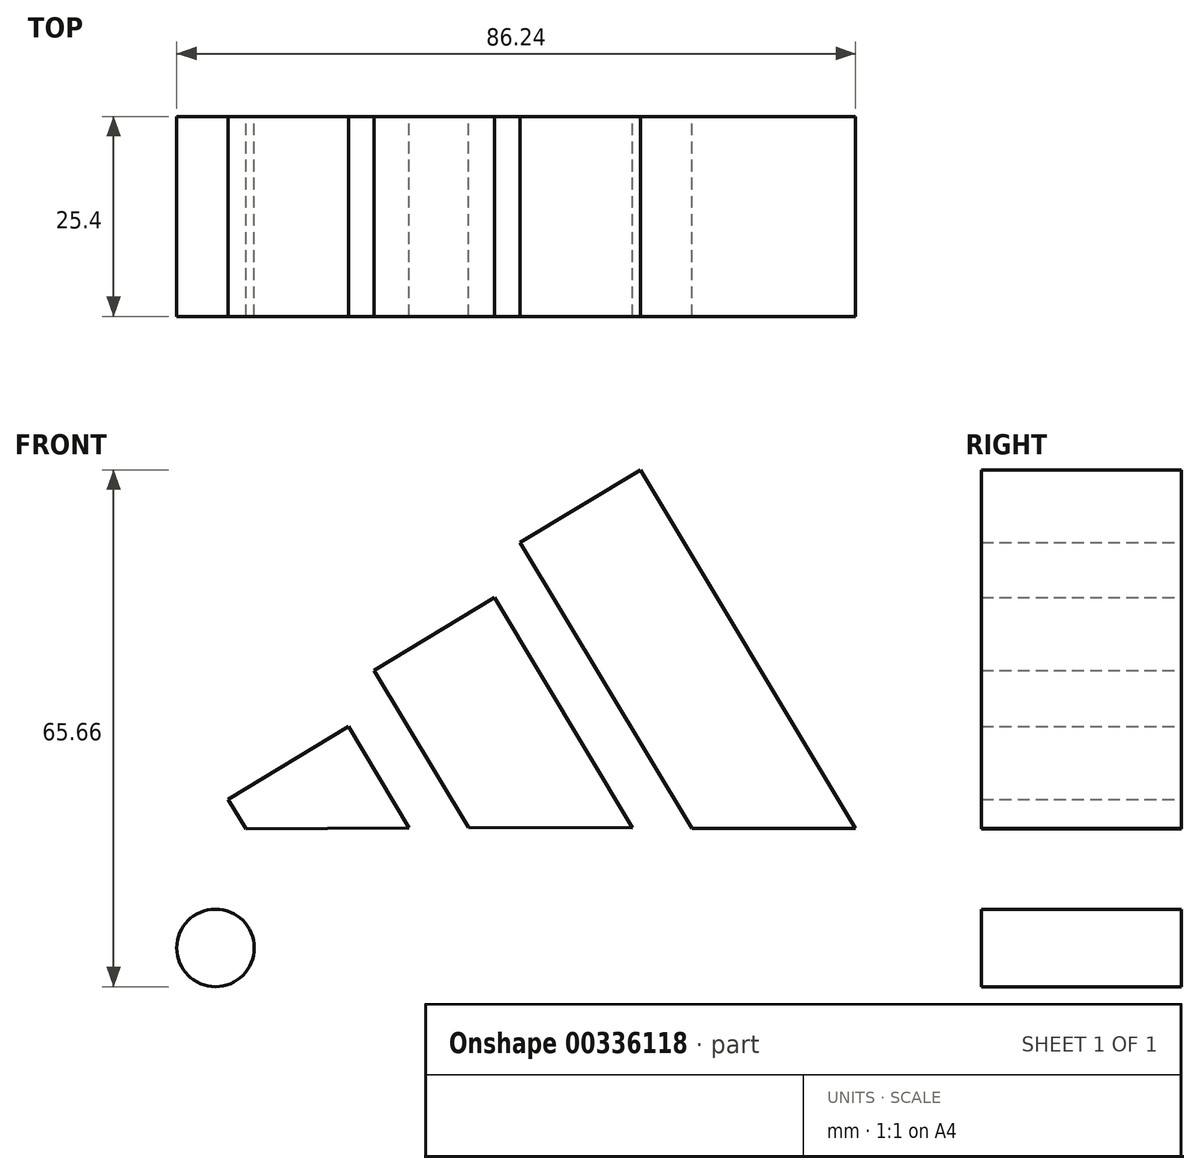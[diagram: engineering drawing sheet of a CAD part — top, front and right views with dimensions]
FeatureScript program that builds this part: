
annotation { "Feature Type Name" : "Feature", "Feature Type Description" : "" }
export const myFeature = defineFeature(function(context is Context, id is Id, definition is map)
    precondition{}
    {
        {
            var Q0;
            Q0=qCreatedBy(makeId("Front.planeOp"),FACE);
            var sketch = newSketch(context, id + "F0", { "sketchPlane" : qUnion([Q0])});
            skLineSegment(sketch, "E0", {"start": v(-25.46, 5.8) * mm, "end": v(-40.77, -3.46) * mm});
            skLineSegment(sketch, "E1", {"start": v(-40.77, -3.46) * mm, "end": v(-38.46, -7.23) * mm});
            skLineSegment(sketch, "E2", {"start": v(-38.46, -7.23) * mm, "end": v(-17.75, -7.13) * mm});
            skLineSegment(sketch, "E3", {"start": v(-17.75, -7.13) * mm, "end": v(-25.46, 5.8) * mm});
            skLineSegment(sketch, "E4", {"start": v(-6.91, 22.2) * mm, "end": v(10.62, -7.1) * mm});
            skLineSegment(sketch, "E5", {"start": v(10.62, -7.1) * mm, "end": v(-10.2, -7.07) * mm});
            skLineSegment(sketch, "E6", {"start": v(-10.2, -7.07) * mm, "end": v(-22.22, 12.9) * mm});
            skLineSegment(sketch, "E7", {"start": v(-22.22, 12.9) * mm, "end": v(-6.91, 22.2) * mm});
            skLineSegment(sketch, "E8", {"start": v(-3.69, 29.15) * mm, "end": v(18.17, -7.16) * mm});
            skLineSegment(sketch, "E9", {"start": v(18.17, -7.16) * mm, "end": v(38.96, -7.16) * mm});
            skLineSegment(sketch, "E10", {"start": v(38.96, -7.16) * mm, "end": v(11.61, 38.39) * mm});
            skLineSegment(sketch, "E11", {"start": v(11.61, 38.39) * mm, "end": v(-3.69, 29.15) * mm});
            skCircle(sketch, "E12", {"center": v(-42.35, -22.35) * mm, "radius": 4.93 * mm});
            skSolve(sketch);
        }
        {
            var Q0;
            Q0=makeQuery(id+"F0.imprint","IMPRINT",FACE,{"disambiguationData":[TD([[makeQuery(id+"F0.imprint","IMPRINT",EDGE,{"derivedFrom":sQuery(id+"F0.wireOp",EDGE,"E0")}),1.0]])]});
            var Q1;
            Q1=makeQuery(id+"F0.imprint","IMPRINT",FACE,{"disambiguationData":[TD([[makeQuery(id+"F0.imprint","IMPRINT",EDGE,{"derivedFrom":sQuery(id+"F0.wireOp",EDGE,"E4")}),-1.0]])]});
            extrude(context, id + "F1", {"entities" : qUnion([Q0, Q1]), "depth" : 1.27 * mm});
        }
        {
            var Q0;
            Q0 = qSketchRegion(id + "F0", true);
            extrude(context, id + "F2", {"entities" : qUnion([Q0]), "operationType" : NewBodyOperationType.ADD, "depth" : 25.4 * mm});
        }
    });
